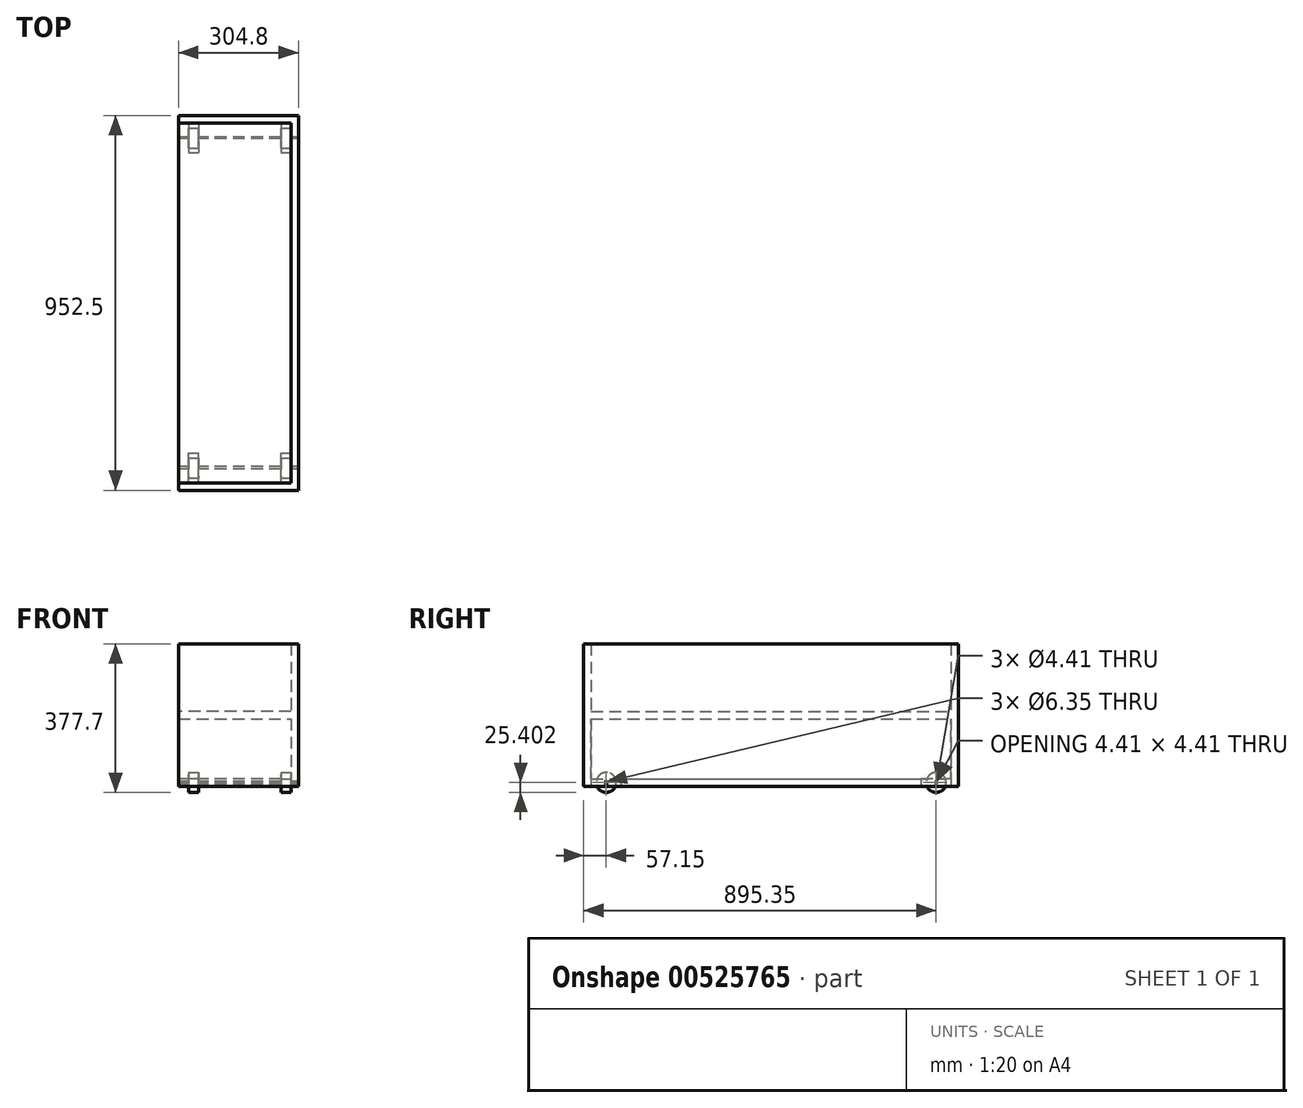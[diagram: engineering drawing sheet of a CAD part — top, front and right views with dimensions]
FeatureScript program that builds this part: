
annotation { "Feature Type Name" : "Feature", "Feature Type Description" : "" }
export const myFeature = defineFeature(function(context is Context, id is Id, definition is map)
    precondition{}
    {
        {
            var Q0;
            Q0=qCreatedBy(makeId("Front.planeOp"),FACE);
            var sketch = newSketch(context, id + "F0", { "sketchPlane" : qUnion([Q0])});
            skLineSegment(sketch, "E0", {"start": v(0, 0) * mm, "end": v(304.8, 0) * mm});
            skLineSegment(sketch, "E1", {"start": v(304.8, 0) * mm, "end": v(304.8, 361.95) * mm});
            skLineSegment(sketch, "E2", {"start": v(304.8, 361.95) * mm, "end": v(0, 361.95) * mm});
            skLineSegment(sketch, "E3", {"start": v(0, 361.95) * mm, "end": v(0, 342.9) * mm});
            skLineSegment(sketch, "E4", {"start": v(0, 342.9) * mm, "end": v(285.75, 342.9) * mm});
            skLineSegment(sketch, "E5", {"start": v(285.75, 342.9) * mm, "end": v(285.75, 190.5) * mm});
            skLineSegment(sketch, "E6", {"start": v(285.75, 190.5) * mm, "end": v(0, 190.5) * mm});
            skLineSegment(sketch, "E7", {"start": v(0, 190.5) * mm, "end": v(0, 171.45) * mm});
            skLineSegment(sketch, "E8", {"start": v(0, 171.45) * mm, "end": v(285.75, 171.45) * mm});
            skLineSegment(sketch, "E9", {"start": v(285.75, 171.45) * mm, "end": v(285.75, 19.05) * mm});
            skLineSegment(sketch, "E10", {"start": v(285.75, 19.05) * mm, "end": v(0, 19.05) * mm});
            skLineSegment(sketch, "E11", {"start": v(0, 19.05) * mm, "end": v(0, 0) * mm});
            skSolve(sketch);
        }
        {
            var Q0;
            Q0 = qSketchRegion(id + "F0", true);
            extrude(context, id + "F1", {"entities" : qUnion([Q0]), "depth" : 914.4 * mm, "offsetDistance" : 25.4 * mm});
        }
        {
            var Q0;
            Q0=makeQuery(id+"F1.opExtrude","CAP_FACE",FACE,{"disambiguationData":[OSD([sQuery(id+"F0.wireOp",EDGE,"E0"),sQuery(id+"F0.wireOp",EDGE,"E1"),sQuery(id+"F0.wireOp",EDGE,"E2"),sQuery(id+"F0.wireOp",EDGE,"E3"),sQuery(id+"F0.wireOp",EDGE,"E4"),sQuery(id+"F0.wireOp",EDGE,"E5"),sQuery(id+"F0.wireOp",EDGE,"E6"),sQuery(id+"F0.wireOp",EDGE,"E7"),sQuery(id+"F0.wireOp",EDGE,"E8"),sQuery(id+"F0.wireOp",EDGE,"E9"),sQuery(id+"F0.wireOp",EDGE,"E10"),sQuery(id+"F0.wireOp",EDGE,"E11")])],"isStart":false});
            var sketch = newSketch(context, id + "F2", { "sketchPlane" : qUnion([Q0])});
            skLineSegment(sketch, "E12.bottom", {"start": v(304.8, 0) * mm, "end": v(0, 0) * mm});
            skLineSegment(sketch, "E12.top", {"start": v(304.8, 361.95) * mm, "end": v(0, 361.95) * mm});
            skLineSegment(sketch, "E12.left", {"start": v(304.8, 0) * mm, "end": v(304.8, 361.95) * mm});
            skLineSegment(sketch, "E12.right", {"start": v(0, 0) * mm, "end": v(0, 361.95) * mm});
            skSolve(sketch);
        }
        {
            var Q0;
            Q0 = qSketchRegion(id + "F2", true);
            extrude(context, id + "F3", {"entities" : qUnion([Q0]), "operationType" : NewBodyOperationType.ADD, "depth" : 19.05 * mm, "offsetDistance" : 25.4 * mm});
        }
        {
            var Q0;
            Q0=makeQuery(id+"F1.opExtrude","CAP_FACE",FACE,{"disambiguationData":[OSD([sQuery(id+"F0.wireOp",EDGE,"E0"),sQuery(id+"F0.wireOp",EDGE,"E1"),sQuery(id+"F0.wireOp",EDGE,"E2"),sQuery(id+"F0.wireOp",EDGE,"E3"),sQuery(id+"F0.wireOp",EDGE,"E4"),sQuery(id+"F0.wireOp",EDGE,"E5"),sQuery(id+"F0.wireOp",EDGE,"E6"),sQuery(id+"F0.wireOp",EDGE,"E7"),sQuery(id+"F0.wireOp",EDGE,"E8"),sQuery(id+"F0.wireOp",EDGE,"E9"),sQuery(id+"F0.wireOp",EDGE,"E10"),sQuery(id+"F0.wireOp",EDGE,"E11")])],"isStart":true});
            var sketch = newSketch(context, id + "F4", { "sketchPlane" : qUnion([Q0])});
            skLineSegment(sketch, "E13.bottom", {"start": v(-304.8, 0) * mm, "end": v(0, 0) * mm});
            skLineSegment(sketch, "E13.top", {"start": v(-304.8, 361.95) * mm, "end": v(0, 361.95) * mm});
            skLineSegment(sketch, "E13.left", {"start": v(-304.8, 0) * mm, "end": v(-304.8, 361.95) * mm});
            skLineSegment(sketch, "E13.right", {"start": v(0, 0) * mm, "end": v(0, 361.95) * mm});
            skSolve(sketch);
        }
        {
            var Q0;
            Q0 = qSketchRegion(id + "F4", true);
            extrude(context, id + "F5", {"entities" : qUnion([Q0]), "operationType" : NewBodyOperationType.ADD, "depth" : 19.05 * mm, "offsetDistance" : 25.4 * mm});
        }
        {
            var Q0;
            Q0=makeQuery(id+"F5.boolean.opBoolean","MERGE",FACE,{"derivedFrom":[makeQuery(id+"F3.boolean.opBoolean","MERGE",FACE,{"derivedFrom":[makeQuery(id+"F1.opExtrude","SWEPT_FACE",FACE,{"disambiguationData":[OSD([sQuery(id+"F0.wireOp",EDGE,"E2")])]}),makeQuery(id+"F3.opExtrude","SWEPT_FACE",FACE,{"disambiguationData":[OSD([sQuery(id+"F2.wireOp",EDGE,"E12.top")])]})]}),makeQuery(id+"F5.opExtrude","SWEPT_FACE",FACE,{"disambiguationData":[OSD([sQuery(id+"F4.wireOp",EDGE,"E13.top")])]})]});
            var sketch = newSketch(context, id + "F6", { "sketchPlane" : qUnion([Q0])});
            skLineSegment(sketch, "E14.bottom", {"start": v(0, -914.4) * mm, "end": v(285.75, -914.4) * mm});
            skLineSegment(sketch, "E14.top", {"start": v(0, 0) * mm, "end": v(285.75, 0) * mm});
            skLineSegment(sketch, "E14.left", {"start": v(0, -914.4) * mm, "end": v(0, 0) * mm});
            skLineSegment(sketch, "E14.right", {"start": v(285.75, -914.4) * mm, "end": v(285.75, 0) * mm});
            skSolve(sketch);
        }
        {
            var Q0;
            Q0 = qSketchRegion(id + "F6", true);
            extrude(context, id + "F7", {"entities" : qUnion([Q0]), "operationType" : NewBodyOperationType.REMOVE, "oppositeDirection" : true, "depth" : 25.4 * mm, "offsetDistance" : 25.4 * mm});
        }
        {
            var Q0;
            Q0=makeQuery(id+"F5.boolean.opBoolean","MERGE",FACE,{"derivedFrom":[makeQuery(id+"F3.boolean.opBoolean","MERGE",FACE,{"derivedFrom":[makeQuery(id+"F1.opExtrude","SWEPT_FACE",FACE,{"disambiguationData":[OSD([sQuery(id+"F0.wireOp",EDGE,"E0")])]}),makeQuery(id+"F3.opExtrude","SWEPT_FACE",FACE,{"disambiguationData":[OSD([sQuery(id+"F2.wireOp",EDGE,"E12.bottom")])]})]}),makeQuery(id+"F5.opExtrude","SWEPT_FACE",FACE,{"disambiguationData":[OSD([sQuery(id+"F4.wireOp",EDGE,"E13.bottom")])]})]});
            var sketch = newSketch(context, id + "F8", { "sketchPlane" : qUnion([Q0])});
            skLineSegment(sketch, "E15.bottom", {"start": v(25.4, 914.4) * mm, "end": v(50.8, 914.4) * mm});
            skLineSegment(sketch, "E15.top", {"start": v(25.4, 838.2) * mm, "end": v(50.8, 838.2) * mm});
            skLineSegment(sketch, "E15.left", {"start": v(25.4, 914.4) * mm, "end": v(25.4, 838.2) * mm});
            skLineSegment(sketch, "E15.right", {"start": v(50.8, 914.4) * mm, "end": v(50.8, 838.2) * mm});
            skLineSegment(sketch, "E16.bottom", {"start": v(260.35, 914.4) * mm, "end": v(285.75, 914.4) * mm});
            skLineSegment(sketch, "E16.top", {"start": v(260.35, 838.2) * mm, "end": v(285.75, 838.2) * mm});
            skLineSegment(sketch, "E16.left", {"start": v(260.35, 914.4) * mm, "end": v(260.35, 838.2) * mm});
            skLineSegment(sketch, "E16.right", {"start": v(285.75, 914.4) * mm, "end": v(285.75, 838.2) * mm});
            skLineSegment(sketch, "E17.bottom", {"start": v(285.75, 0) * mm, "end": v(260.35, 0) * mm});
            skLineSegment(sketch, "E17.top", {"start": v(285.75, 76.2) * mm, "end": v(260.35, 76.2) * mm});
            skLineSegment(sketch, "E17.left", {"start": v(285.75, 0) * mm, "end": v(285.75, 76.2) * mm});
            skLineSegment(sketch, "E17.right", {"start": v(260.35, 0) * mm, "end": v(260.35, 76.2) * mm});
            skLineSegment(sketch, "E18.bottom", {"start": v(50.8, 0) * mm, "end": v(25.4, 0) * mm});
            skLineSegment(sketch, "E18.top", {"start": v(50.8, 76.2) * mm, "end": v(25.4, 76.2) * mm});
            skLineSegment(sketch, "E18.left", {"start": v(50.8, 0) * mm, "end": v(50.8, 76.2) * mm});
            skLineSegment(sketch, "E18.right", {"start": v(25.4, 0) * mm, "end": v(25.4, 76.2) * mm});
            skSolve(sketch);
        }
        {
            var Q0;
            Q0 = qSketchRegion(id + "F8", true);
            extrude(context, id + "F9", {"entities" : qUnion([Q0]), "operationType" : NewBodyOperationType.REMOVE, "oppositeDirection" : true, "depth" : 25.4 * mm, "offsetDistance" : 25.4 * mm});
        }
        {
            var Q0;
            Q0=makeQuery(id+"F5.boolean.opBoolean","MERGE",FACE,{"derivedFrom":[makeQuery(id+"F3.boolean.opBoolean","MERGE",FACE,{"derivedFrom":[makeQuery(id+"F1.opExtrude","SWEPT_FACE",FACE,{"disambiguationData":[OSD([sQuery(id+"F0.wireOp",EDGE,"E3")])]}),makeQuery(id+"F1.opExtrude","SWEPT_FACE",FACE,{"disambiguationData":[OSD([sQuery(id+"F0.wireOp",EDGE,"E7")])]}),makeQuery(id+"F1.opExtrude","SWEPT_FACE",FACE,{"disambiguationData":[OSD([sQuery(id+"F0.wireOp",EDGE,"E11")])]}),makeQuery(id+"F3.opExtrude","SWEPT_FACE",FACE,{"disambiguationData":[OSD([sQuery(id+"F2.wireOp",EDGE,"E12.right")])]})]}),makeQuery(id+"F5.opExtrude","SWEPT_FACE",FACE,{"disambiguationData":[OSD([sQuery(id+"F4.wireOp",EDGE,"E13.right")])]})]});
            var sketch = newSketch(context, id + "F10", { "sketchPlane" : qUnion([Q0])});
            skCircle(sketch, "E19", {"center": v(876.3, 9.65) * mm, "radius": 3.18 * mm});
            skCircle(sketch, "E20", {"center": v(38.1, 9.65) * mm, "radius": 2.2 * mm});
            skSolve(sketch);
        }
        {
            var Q0;
            Q0 = qSketchRegion(id + "F10", true);
            extrude(context, id + "F11", {"entities" : qUnion([Q0]), "operationType" : NewBodyOperationType.REMOVE, "endBound" : BoundingType.THROUGH_ALL, "oppositeDirection" : true, "depth" : 25.4 * mm, "offsetDistance" : 25.4 * mm});
        }
        {
            var Q0;
            Q0=makeQuery(id+"F9.boolean.opBoolean","COPY",FACE,{"derivedFrom":makeQuery(id+"F9.opExtrude","SWEPT_FACE",FACE,{"disambiguationData":[OSD([sQuery(id+"F8.wireOp",EDGE,"E15.right")])]})});
            var sketch = newSketch(context, id + "F12", { "sketchPlane" : qUnion([Q0])});
            skCircle(sketch, "E21", {"center": v(876.3, 9.65) * mm, "radius": 25.4 * mm});
            skCircle(sketch, "E22", {"center": v(38.1, 9.65) * mm, "radius": 25.4 * mm});
            skSolve(sketch);
        }
        {
            var Q0;
            Q0 = qSketchRegion(id + "F12", true);
            extrude(context, id + "F13", {"entities" : qUnion([Q0]), "depth" : 25.4 * mm, "offsetDistance" : 25.4 * mm});
        }
        {
            var Q0;
            Q0=makeQuery(id+"F9.boolean.opBoolean","MERGE",FACE,{"derivedFrom":[makeQuery(id+"F1.opExtrude","SWEPT_FACE",FACE,{"disambiguationData":[OSD([sQuery(id+"F0.wireOp",EDGE,"E9")])]}),makeQuery(id+"F9.opExtrude","SWEPT_FACE",FACE,{"disambiguationData":[OSD([sQuery(id+"F8.wireOp",EDGE,"E16.right")])]}),makeQuery(id+"F9.opExtrude","SWEPT_FACE",FACE,{"disambiguationData":[OSD([sQuery(id+"F8.wireOp",EDGE,"E17.left")])]})]});
            var sketch = newSketch(context, id + "F14", { "sketchPlane" : qUnion([Q0])});
            skCircle(sketch, "E23", {"center": v(876.3, 9.65) * mm, "radius": 25.4 * mm});
            skCircle(sketch, "E24", {"center": v(38.1, 9.65) * mm, "radius": 25.4 * mm});
            skSolve(sketch);
        }
        {
            var Q0;
            Q0 = qSketchRegion(id + "F14", true);
            extrude(context, id + "F15", {"entities" : qUnion([Q0]), "depth" : 25.4 * mm, "offsetDistance" : 25.4 * mm});
        }
    });
